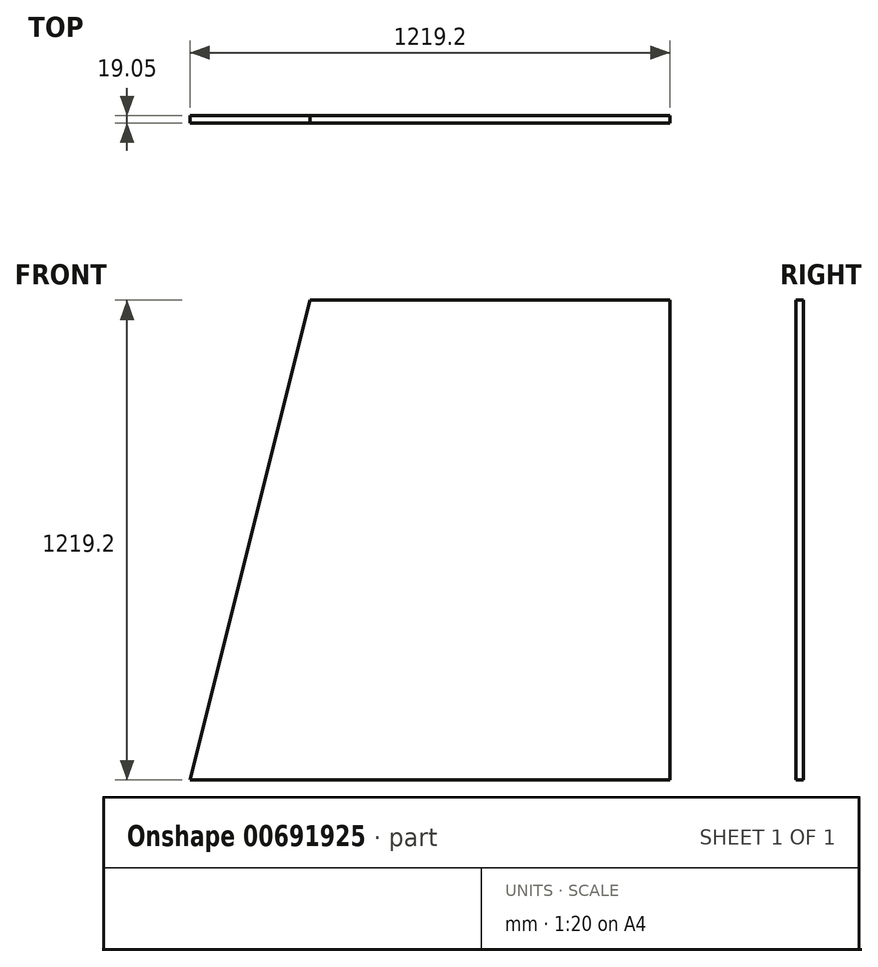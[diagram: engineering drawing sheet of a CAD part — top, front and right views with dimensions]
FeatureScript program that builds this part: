
annotation { "Feature Type Name" : "Feature", "Feature Type Description" : "" }
export const myFeature = defineFeature(function(context is Context, id is Id, definition is map)
    precondition{}
    {
        {
            var Q0;
            Q0=qCreatedBy(makeId("Front.planeOp"),FACE);
            var sketch = newSketch(context, id + "F0", { "sketchPlane" : qUnion([Q0])});
            skLineSegment(sketch, "E0", {"start": v(0, 0) * mm, "end": v(1219.2, 0) * mm});
            skLineSegment(sketch, "E1", {"start": v(1219.2, 0) * mm, "end": v(1219.2, 1219.2) * mm});
            skLineSegment(sketch, "E2", {"start": v(1219.2, 1219.2) * mm, "end": v(304.8, 1219.2) * mm});
            skLineSegment(sketch, "E3", {"start": v(304.8, 1219.2) * mm, "end": v(0, 0) * mm});
            skSolve(sketch);
        }
        {
            var Q0;
            Q0 = qSketchRegion(id + "F0", true);
            extrude(context, id + "F1", {"entities" : qUnion([Q0]), "depth" : 19.05 * mm, "offsetDistance" : 25.4 * mm});
        }
    });
